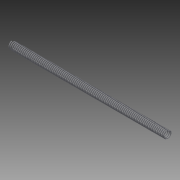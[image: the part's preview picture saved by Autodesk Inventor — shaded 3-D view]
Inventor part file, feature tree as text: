
AUTODESK INVENTOR PART (.ipt)
format: ipt  version: 2014 (Build 180170000, 170)  size: 774,144 bytes
history: native  units: in
note: dims shown in document units (in); Inventor stores cm internally (conversion verified against a paired STEP export)
features: helix x1, sketch x1
ambient origin geometry x8: Origin, YZ Plane, XZ Plane, XY Plane, X Axis, Y Axis, Z Axis, Center Point
bodies: Solid1 (feature_tree)
feature tree (2):
  helix  "Coil1"  [1 undecoded]
  sketch  "Sketch1"  dims[d1=0.5in d2=0.25in d3=1.0in d4=37.7953in d5=0.0in d6=90.0deg d7=90.0deg d8=0.0in d9=0.0in]
note: 1 required parameter value undecoded (feature->parameter linkage not recoverable at this tier; creation-order binding heuristic only, values carry confidence <= 0.55)
